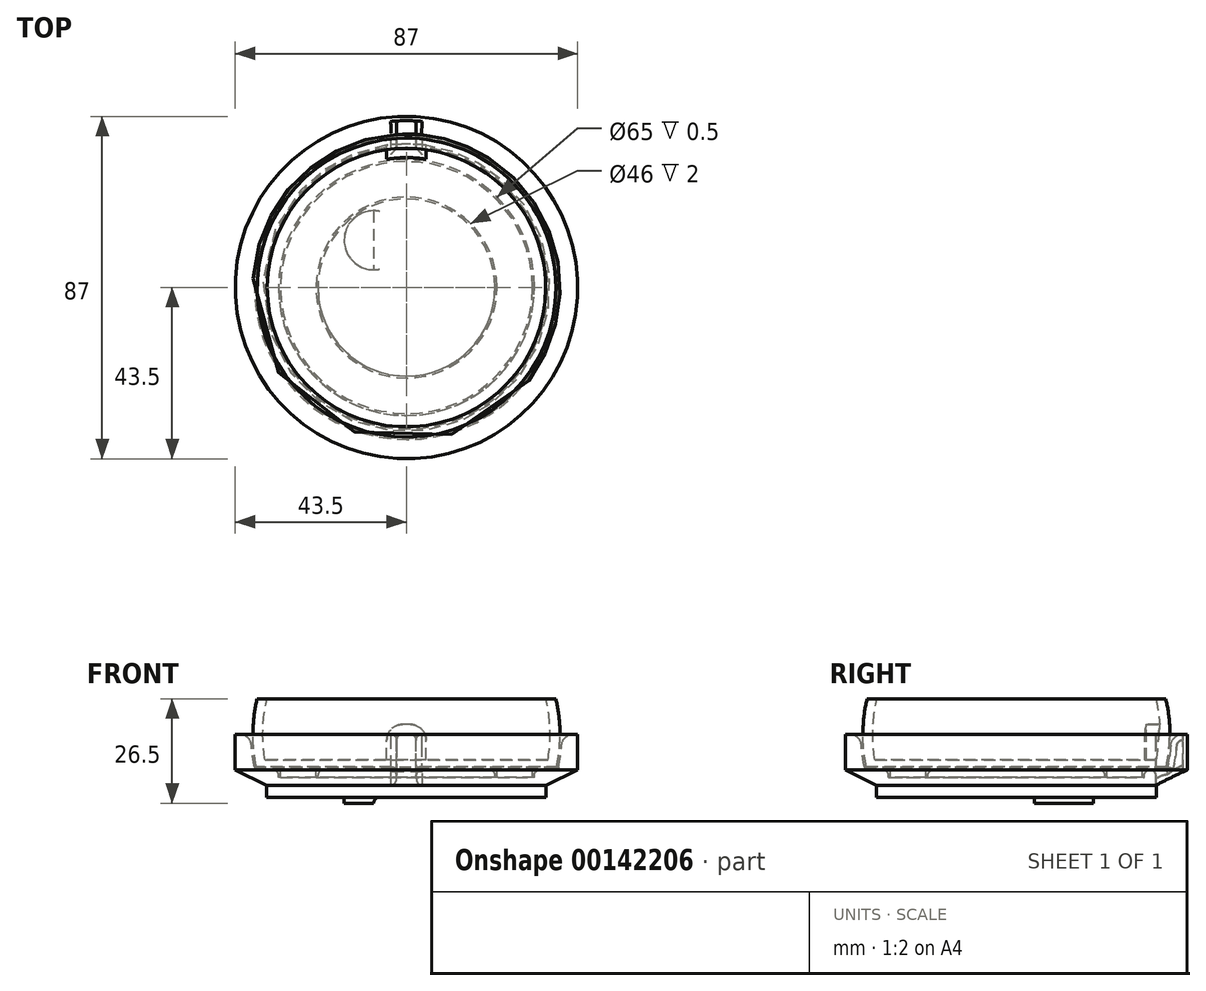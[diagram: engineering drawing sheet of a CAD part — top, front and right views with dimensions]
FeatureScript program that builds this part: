
annotation { "Feature Type Name" : "Feature", "Feature Type Description" : "" }
export const myFeature = defineFeature(function(context is Context, id is Id, definition is map)
    precondition{}
    {
        {
            var Q0;
            Q0=qCreatedBy(makeId("Front.planeOp"),FACE);
            var sketch = newSketch(context, id + "F0", { "sketchPlane" : qUnion([Q0])});
            skArc(sketch, "E0", {"start": v(37.95, -9) * mm, "mid": v(39, 0) * mm, "end": v(37.95, 9) * mm});
            skLineSegment(sketch, "E1", {"start": v(-37.95, 9) * mm, "end": v(37.95, 9) * mm});
            skLineSegment(sketch, "E2.MirrorCS", {"start": v(-37.95, -9) * mm, "end": v(37.95, -9) * mm});
            skArc(sketch, "E3.trimOffspring", {"start": v(-37.95, 9) * mm, "mid": v(-39, 0) * mm, "end": v(-37.95, -9) * mm});
            skLineSegment(sketch, "E4", {"start": v(0, 9) * mm, "end": v(0, -9) * mm});
            skSolve(sketch);
        }
        {
            var Q0;
            {var subQ0=sQuery(id+"F0.wireOp",EDGE,"E0");Q0=makeQuery(id+"F0.imprint","IMPRINT",FACE,{"disambiguationData":[TD([[makeQuery(id+"F0.imprint","IMPRINT",EDGE,{"derivedFrom":subQ0}),1.0]])]});}
            var Q1;
            Q1=sQuery(id+"F0.wireOp",EDGE,"E4");
            revolve(context, id + "F1", {"entities" : qUnion([Q0]), "axis" : qUnion([Q1]), "revolveType" : RevolveType.FULL});
        }
        {
            var Q0;
            Q0=makeQuery(id+"F1.opRevolve","SWEPT_EDGE",EDGE,{"disambiguationData":[OSD([sQuery(id+"F0.wireOp",EDGE,"E0"),sQuery(id+"F0.wireOp",EDGE,"E2.MirrorCS")])]});
            fillet(context, id + "F2", {"entities" : qUnion([Q0]), "radius" : 1 * mm, "tangentPropagation" : true, "allowEdgeOverflow" : false});
        }
        {
            var Q0;
            Q0=makeQuery(id+"F1.opRevolve","SWEPT_FACE",FACE,{"disambiguationData":[OSD([sQuery(id+"F0.wireOp",EDGE,"E2.MirrorCS")])]});
            var sketch = newSketch(context, id + "F3", { "sketchPlane" : qUnion([Q0])});
            skCircle(sketch, "E5.0", {"center": v(0, 0) * mm, "radius": 37.15 * mm});
            skCircle(sketch, "E6", {"center": v(0, 0) * mm, "radius": 23 * mm});
            skCircle(sketch, "E7", {"center": v(0, 0) * mm, "radius": 32 * mm});
            skSolve(sketch);
        }
        {
            var Q0;
            Q0=makeQuery(id+"F3.imprint","IMPRINT",FACE,{"disambiguationData":[TD([[makeQuery(id+"F3.imprint","IMPRINT",EDGE,{"derivedFrom":sQuery(id+"F3.wireOp",EDGE,"E6")}),-1.0]])]});
            extrude(context, id + "F4", {"entities" : qUnion([Q0]), "depth" : 2 * mm});
        }
        {
            var Q0;
            Q0=qCreatedBy(makeId("Front.planeOp"),FACE);
            var sketch = newSketch(context, id + "F5", { "sketchPlane" : qUnion([Q0])});
            skLineSegment(sketch, "E8.0", {"start": v(38.27, -9) * mm, "end": v(0, -9) * mm});
            skLineSegment(sketch, "E9", {"start": v(32.5, -9) * mm, "end": v(32.5, -11) * mm});
            skLineSegment(sketch, "E10.0", {"start": v(32.5, -11) * mm, "end": v(22.5, -11) * mm});
            skLineSegment(sketch, "E11", {"start": v(0, 0) * mm, "end": v(39.5, 0) * mm});
            skLineSegment(sketch, "E12", {"start": v(39.5, 0) * mm, "end": v(43.5, 0) * mm});
            skLineSegment(sketch, "E13", {"start": v(43.5, 0) * mm, "end": v(43.5, -9) * mm});
            skLineSegment(sketch, "E14", {"start": v(0, 0) * mm, "end": v(0, -23) * mm});
            skLineSegment(sketch, "E15", {"start": v(22.5, -9) * mm, "end": v(22.5, -11) * mm});
            skArc(sketch, "E16.0", {"start": v(38.61, -8.32) * mm, "mid": v(39.28, -4.18) * mm, "end": v(39.5, 0) * mm});
            skArc(sketch, "E16.1", {"start": v(38.27, -9) * mm, "mid": v(38.49, -8.68) * mm, "end": v(38.61, -8.32) * mm});
            skPoint(sketch, "E17.orphan", {"position": v(37.15, -9) * mm});
            skLineSegment(sketch, "E18", {"start": v(35.5, -21) * mm, "end": v(35.5, -13) * mm});
            skLineSegment(sketch, "E19", {"start": v(35.5, -21) * mm, "end": v(43.5, -21) * mm});
            skLineSegment(sketch, "E20", {"start": v(43.5, -21) * mm, "end": v(43.5, -23) * mm});
            skLineSegment(sketch, "E21", {"start": v(43.5, -23) * mm, "end": v(0, -23) * mm});
            skPoint(sketch, "E22.visualSharp", {"position": v(35.5, -21) * mm});
            skLineSegment(sketch, "E23", {"start": v(43.5, -9) * mm, "end": v(35.5, -13) * mm});
            skSolve(sketch);
        }
        {
            var Q0;
            {var subQ1=sQuery(id+"F5.wireOp",EDGE,"E9");Q0=makeQuery(id+"F5.imprint","IMPRINT",FACE,{"disambiguationData":[TD([[makeQuery(id+"F5.imprint","IMPRINT",EDGE,{"derivedFrom":subQ1}),1.0]])]});}
            var Q1;
            Q1=sQuery(id+"F5.wireOp",EDGE,"E14");
            revolve(context, id + "F6", {"entities" : qUnion([Q0]), "axis" : qUnion([Q1]), "revolveType" : RevolveType.FULL});
        }
        {
            var Q0;
            Q0=makeQuery(id+"F6.opRevolve","SWEPT_EDGE",EDGE,{"disambiguationData":[OSD([sQuery(id+"F5.wireOp",EDGE,"E12"),sQuery(id+"F5.wireOp",EDGE,"E16.0")])]});
            fillet(context, id + "F7", {"entities" : qUnion([Q0]), "radius" : 3 * mm, "tangentPropagation" : true, "allowEdgeOverflow" : false});
        }
        {
            var Q0;
            Q0=makeQuery(id+"F6.opRevolve","SWEPT_EDGE",EDGE,{"disambiguationData":[OSD([sQuery(id+"F5.wireOp",EDGE,"E8.0"),sQuery(id+"F5.wireOp",EDGE,"E9")])]});
            var Q1;
            Q1=makeQuery(id+"F6.opRevolve","SWEPT_EDGE",EDGE,{"disambiguationData":[OSD([sQuery(id+"F5.wireOp",EDGE,"E8.0"),sQuery(id+"F5.wireOp",EDGE,"E15")])]});
            fillet(context, id + "F8", {"entities" : qUnion([Q0, Q1]), "radius" : 1.5 * mm, "tangentPropagation" : true, "allowEdgeOverflow" : false});
        }
        {
            var Q0;
            Q0=makeQuery(id+"F6.opRevolve","SWEPT_FACE",FACE,{"disambiguationData":[OSD([sQuery(id+"F5.wireOp",EDGE,"E12")])]});
            var sketch = newSketch(context, id + "F9", { "sketchPlane" : qUnion([Q0])});
            skArc(sketch, "E24.0", {"start": v(2.47, 43.43) * mm, "mid": v(-0.02, 43.5) * mm, "end": v(-2.52, 43.43) * mm});
            skLineSegment(sketch, "E25.trimOffspring", {"start": v(-7.5, 31.62) * mm, "end": v(-7.5, -31.62) * mm});
            skLineSegment(sketch, "E26.trimOffspring", {"start": v(7.5, 31.62) * mm, "end": v(7.5, -31.62) * mm});
            skLineSegment(sketch, "E27.left", {"start": v(2.5, 32.4) * mm, "end": v(2.47, 43.43) * mm});
            skLineSegment(sketch, "E27.right", {"start": v(-2.5, 32.4) * mm, "end": v(-2.52, 43.43) * mm});
            skPoint(sketch, "E28.orphan", {"position": v(7.5, 36.76) * mm});
            skArc(sketch, "E29.0", {"start": v(-2.5, 32.4) * mm, "mid": v(-5.01, 32.11) * mm, "end": v(-7.5, 31.62) * mm});
            skArc(sketch, "E30.trimOffspring", {"start": v(7.5, 31.62) * mm, "mid": v(5.01, 32.11) * mm, "end": v(2.5, 32.4) * mm});
            skArc(sketch, "E31.trimOffspring", {"start": v(-7.5, -31.62) * mm, "mid": v(0, -32.5) * mm, "end": v(7.5, -31.62) * mm});
            skCircle(sketch, "E32.0", {"center": v(0, 0) * mm, "radius": 35.5 * mm});
            skSolve(sketch);
        }
        {
            var Q0;
            {var subQ0=sQuery(id+"F9.wireOp",EDGE,"E32.0");var subQ1=sQuery(id+"F9.wireOp",EDGE,"E27.left");var subQ2=makeQuery(id+"F9.imprint","INTERSECT",VERTEX,{"derivedFrom":[subQ1,subQ0]});Q0=makeQuery(id+"F9.imprint","IMPRINT",FACE,{"disambiguationData":[TD([[makeQuery(id+"F9.imprint","IMPRINT",EDGE,{"disambiguationData":[TD([[subQ2,-1.0]])],"derivedFrom":subQ0}),-1.0]])]});}
            var Q1;
            {var subQ0=sQuery(id+"F9.wireOp",EDGE,"E24.0");Q1=makeQuery(id+"F9.imprint","IMPRINT",FACE,{"disambiguationData":[TD([[makeQuery(id+"F9.imprint","IMPRINT",EDGE,{"derivedFrom":subQ0}),1.0]])]});}
            extrude(context, id + "F10", {"entities" : qUnion([Q0, Q1]), "operationType" : NewBodyOperationType.REMOVE, "oppositeDirection" : true, "depth" : 14 * mm});
        }
        {
            var Q0;
            {var subQ0=sQuery(id+"F5.wireOp",EDGE,"E8.0");Q0=makeQuery(id+"F10.boolean.opBoolean","INTERSECT",EDGE,{"derivedFrom":[makeQuery(id+"F6.opRevolve","SWEPT_FACE",FACE,{"disambiguationData":[OSD([subQ0]),TDD([makeQuery(id+"F5.imprint","IMPRINT",EDGE,{"disambiguationData":[TD([[makeQuery(id+"F5.imprint","INTERSECT",VERTEX,{"derivedFrom":[subQ0,sQuery(id+"F5.wireOp",EDGE,"E16.1")]}),-1.0]])],"derivedFrom":subQ0})])]}),makeQuery(id+"F10.opExtrude","SWEPT_FACE",FACE,{"disambiguationData":[OSD([sQuery(id+"F9.wireOp",EDGE,"E32.0")])]})]});}
            var Q1;
            {var subQ0=sQuery(id+"F5.wireOp",EDGE,"E8.0");Q1=makeQuery(id+"F10.boolean.opBoolean","INTERSECT",EDGE,{"derivedFrom":[makeQuery(id+"F6.opRevolve","SWEPT_FACE",FACE,{"disambiguationData":[OSD([subQ0]),TDD([makeQuery(id+"F5.imprint","IMPRINT",EDGE,{"disambiguationData":[TD([[makeQuery(id+"F5.imprint","INTERSECT",VERTEX,{"derivedFrom":[subQ0,sQuery(id+"F5.wireOp",EDGE,"E16.1")]}),-1.0]])],"derivedFrom":subQ0})])]}),makeQuery(id+"F10.opExtrude","SWEPT_FACE",FACE,{"disambiguationData":[OSD([sQuery(id+"F9.wireOp",EDGE,"E27.right")])]})]});}
            var Q2;
            Q2=makeQuery(id+"F10.boolean.opBoolean","INTERSECT",EDGE,{"derivedFrom":[makeQuery(id+"F6.opRevolve","SWEPT_FACE",FACE,{"disambiguationData":[OSD([sQuery(id+"F5.wireOp",EDGE,"E16.1")])]}),makeQuery(id+"F10.opExtrude","SWEPT_FACE",FACE,{"disambiguationData":[OSD([sQuery(id+"F9.wireOp",EDGE,"E27.right")])]})]});
            var Q3;
            Q3=makeQuery(id+"F10.boolean.opBoolean","INTERSECT",EDGE,{"derivedFrom":[makeQuery(id+"F6.opRevolve","SWEPT_FACE",FACE,{"disambiguationData":[OSD([sQuery(id+"F5.wireOp",EDGE,"E16.0")])]}),makeQuery(id+"F10.opExtrude","SWEPT_FACE",FACE,{"disambiguationData":[OSD([sQuery(id+"F9.wireOp",EDGE,"E27.right")])]})]});
            var Q4;
            {var subQ0=sQuery(id+"F5.wireOp",EDGE,"E8.0");Q4=makeQuery(id+"F10.boolean.opBoolean","INTERSECT",EDGE,{"derivedFrom":[makeQuery(id+"F6.opRevolve","SWEPT_FACE",FACE,{"disambiguationData":[OSD([subQ0]),TDD([makeQuery(id+"F5.imprint","IMPRINT",EDGE,{"disambiguationData":[TD([[makeQuery(id+"F5.imprint","INTERSECT",VERTEX,{"derivedFrom":[subQ0,sQuery(id+"F5.wireOp",EDGE,"E16.1")]}),-1.0]])],"derivedFrom":subQ0})])]}),makeQuery(id+"F10.opExtrude","SWEPT_FACE",FACE,{"disambiguationData":[OSD([sQuery(id+"F9.wireOp",EDGE,"E27.left")])]})]});}
            var Q5;
            Q5=makeQuery(id+"F10.boolean.opBoolean","INTERSECT",EDGE,{"derivedFrom":[makeQuery(id+"F6.opRevolve","SWEPT_FACE",FACE,{"disambiguationData":[OSD([sQuery(id+"F5.wireOp",EDGE,"E16.1")])]}),makeQuery(id+"F10.opExtrude","SWEPT_FACE",FACE,{"disambiguationData":[OSD([sQuery(id+"F9.wireOp",EDGE,"E27.left")])]})]});
            var Q6;
            Q6=makeQuery(id+"F10.boolean.opBoolean","INTERSECT",EDGE,{"derivedFrom":[makeQuery(id+"F6.opRevolve","SWEPT_FACE",FACE,{"disambiguationData":[OSD([sQuery(id+"F5.wireOp",EDGE,"E16.0")])]}),makeQuery(id+"F10.opExtrude","SWEPT_FACE",FACE,{"disambiguationData":[OSD([sQuery(id+"F9.wireOp",EDGE,"E27.left")])]})]});
            var Q7;
            Q7=makeQuery(id+"F10.boolean.opBoolean","INTERSECT",EDGE,{"derivedFrom":[makeQuery(id+"F7.opFillet","BLEND_FACE",FACE,{"disambiguationData":[OSD([sQuery(id+"F5.wireOp",EDGE,"E11"),sQuery(id+"F5.wireOp",EDGE,"E12"),sQuery(id+"F5.wireOp",EDGE,"E16.0")])]}),makeQuery(id+"F10.opExtrude","SWEPT_FACE",FACE,{"disambiguationData":[OSD([sQuery(id+"F9.wireOp",EDGE,"E27.left")])]})]});
            var Q8;
            Q8=makeQuery(id+"F10.boolean.opBoolean","COPY",EDGE,{"derivedFrom":makeQuery(id+"F10.opExtrude","CAP_EDGE",EDGE,{"disambiguationData":[OSD([sQuery(id+"F9.wireOp",EDGE,"E27.left")])],"isStart":true})});
            var Q9;
            Q9=makeQuery(id+"F10.boolean.opBoolean","INTERSECT",EDGE,{"derivedFrom":[makeQuery(id+"F6.opRevolve","SWEPT_FACE",FACE,{"disambiguationData":[OSD([sQuery(id+"F5.wireOp",EDGE,"E23")])]}),makeQuery(id+"F10.opExtrude","SWEPT_FACE",FACE,{"disambiguationData":[OSD([sQuery(id+"F9.wireOp",EDGE,"E27.right")])]})]});
            var Q10;
            Q10=makeQuery(id+"F10.boolean.opBoolean","INTERSECT",EDGE,{"derivedFrom":[makeQuery(id+"F6.opRevolve","SWEPT_FACE",FACE,{"disambiguationData":[OSD([sQuery(id+"F5.wireOp",EDGE,"E23")])]}),makeQuery(id+"F10.opExtrude","SWEPT_FACE",FACE,{"disambiguationData":[OSD([sQuery(id+"F9.wireOp",EDGE,"E27.left")])]})]});
            var Q11;
            Q11=makeQuery(id+"F10.boolean.opBoolean","INTERSECT",EDGE,{"derivedFrom":[makeQuery(id+"F7.opFillet","BLEND_FACE",FACE,{"disambiguationData":[OSD([sQuery(id+"F5.wireOp",EDGE,"E11"),sQuery(id+"F5.wireOp",EDGE,"E12"),sQuery(id+"F5.wireOp",EDGE,"E16.0")])]}),makeQuery(id+"F10.opExtrude","SWEPT_FACE",FACE,{"disambiguationData":[OSD([sQuery(id+"F9.wireOp",EDGE,"E27.right")])]})]});
            var Q12;
            Q12=makeQuery(id+"F10.boolean.opBoolean","COPY",EDGE,{"derivedFrom":makeQuery(id+"F10.opExtrude","CAP_EDGE",EDGE,{"disambiguationData":[OSD([sQuery(id+"F9.wireOp",EDGE,"E27.right")])],"isStart":true})});
            fillet(context, id + "F11", {"entities" : qUnion([Q0, Q1, Q2, Q3, Q4, Q5, Q6, Q7, Q8, Q9, Q10, Q11, Q12]), "radius" : 1.5 * mm, "tangentPropagation" : true, "allowEdgeOverflow" : false});
        }
        {
            var Q0;
            Q0=makeQuery(id+"F6.opRevolve","SWEPT_FACE",FACE,{"disambiguationData":[OSD([sQuery(id+"F5.wireOp",EDGE,"E19")])]});
            var sketch = newSketch(context, id + "F12", { "sketchPlane" : qUnion([Q0])});
            skCircle(sketch, "E33.0", {"center": v(0, 0) * mm, "radius": 43.5 * mm});
            skCircle(sketch, "E34.0", {"center": v(0, 0) * mm, "radius": 35.5 * mm});
            skLineSegment(sketch, "E35", {"start": v(2.5, 35.41) * mm, "end": v(2.5, 43.43) * mm});
            skLineSegment(sketch, "E36", {"start": v(-2.5, 35.41) * mm, "end": v(-2.5, 43.43) * mm});
            skSolve(sketch);
        }
        {
            var Q0;
            {var subQ0=sQuery(id+"F12.wireOp",EDGE,"E35");Q0=makeQuery(id+"F12.imprint","IMPRINT",FACE,{"disambiguationData":[TD([[makeQuery(id+"F12.imprint","IMPRINT",EDGE,{"derivedFrom":subQ0}),1.0]])]});}
            extrude(context, id + "F13", {"entities" : qUnion([Q0]), "operationType" : NewBodyOperationType.REMOVE, "oppositeDirection" : true, "depth" : 25 * mm});
        }
        {
            var Q0;
            Q0=makeQuery(id+"F6.opRevolve","SWEPT_FACE",FACE,{"disambiguationData":[OSD([sQuery(id+"F5.wireOp",EDGE,"E21")])]});
            var sketch = newSketch(context, id + "F14", { "sketchPlane" : qUnion([Q0])});
            skLineSegment(sketch, "E37", {"start": v(-2.5, -43.43) * mm, "end": v(-2.5, -28.43) * mm});
            skLineSegment(sketch, "E38", {"start": v(2.5, -43.43) * mm, "end": v(2.5, -28.43) * mm});
            skLineSegment(sketch, "E39", {"start": v(-2.5, -43.43) * mm, "end": v(2.5, -43.43) * mm});
            skPoint(sketch, "E40", {"position": v(0, -35.5) * mm});
            skLineSegment(sketch, "E41", {"start": v(0, -43.43) * mm, "end": v(0, 10.29) * mm, "construction": true});
            skArc(sketch, "E42", {"start": v(-8.32, -20.49) * mm, "mid": v(-4.92, -27.2) * mm, "end": v(2.5, -28.43) * mm});
            skLineSegment(sketch, "E43", {"start": v(-8.33, -20.49) * mm, "end": v(-8.33, -3.56) * mm});
            skLineSegment(sketch, "E44", {"start": v(8.32, -20.49) * mm, "end": v(8.32, -3.56) * mm});
            skLineSegment(sketch, "E45", {"start": v(-8.32, -3.56) * mm, "end": v(-6.25, -3.56) * mm});
            skLineSegment(sketch, "E46", {"start": v(-6.25, -3.56) * mm, "end": v(-6.25, 8.94) * mm});
            skLineSegment(sketch, "E47", {"start": v(-6.25, 8.94) * mm, "end": v(6.25, 8.94) * mm});
            skLineSegment(sketch, "E48", {"start": v(6.25, 8.94) * mm, "end": v(6.25, -3.56) * mm});
            skLineSegment(sketch, "E49.trimOffspring", {"start": v(6.25, -3.56) * mm, "end": v(8.32, -3.56) * mm});
            skArc(sketch, "E50.trimOffspring", {"start": v(2.5, -28.43) * mm, "mid": v(6.71, -25.41) * mm, "end": v(8.32, -20.49) * mm});
            skArc(sketch, "E51", {"start": v(-8.33, -4.52) * mm, "mid": v(-15.82, -12.02) * mm, "end": v(-8.32, -19.52) * mm});
            skSolve(sketch);
        }
        {
            var Q0;
            {var subQ0=sQuery(id+"F14.wireOp",EDGE,"E43");Q0=makeQuery(id+"F14.imprint","IMPRINT",FACE,{"disambiguationData":[TD([[makeQuery(id+"F14.imprint","IMPRINT",EDGE,{"derivedFrom":subQ0}),-1.0]])]});}
            extrude(context, id + "F15", {"entities" : qUnion([Q0]), "operationType" : NewBodyOperationType.REMOVE, "oppositeDirection" : true, "depth" : 7 * mm});
        }
        {
            var Q0;
            {var subQ1=makeQuery(id+"F13.boolean.opBoolean","INTERSECT",EDGE,{"derivedFrom":[makeQuery(id+"F6.opRevolve","SWEPT_FACE",FACE,{"disambiguationData":[OSD([sQuery(id+"F5.wireOp",EDGE,"E21")])]}),makeQuery(id+"F13.opExtrude","SWEPT_FACE",FACE,{"disambiguationData":[OSD([sQuery(id+"F12.wireOp",EDGE,"E34.0")])]})]});Q0=makeQuery(id+"F14.imprint","IMPRINT",FACE,{"disambiguationData":[TD([[makeQuery(id+"F14.imprint","IMPRINT",EDGE,{"derivedFrom":subQ1}),1.0]])]});}
            extrude(context, id + "F16", {"entities" : qUnion([Q0]), "operationType" : NewBodyOperationType.REMOVE, "oppositeDirection" : true, "depth" : 6 * mm});
        }
        {
            var Q0;
            {var subQ0=sQuery(id+"F14.wireOp",EDGE,"E51");Q0=makeQuery(id+"F14.imprint","IMPRINT",FACE,{"disambiguationData":[TD([[makeQuery(id+"F14.imprint","IMPRINT",EDGE,{"derivedFrom":subQ0}),1.0]])]});}
            extrude(context, id + "F17", {"entities" : qUnion([Q0]), "oppositeDirection" : true, "depth" : 5.5 * mm});
        }
        {
            var Q0;
            Q0=qCreatedBy(makeId("Front.planeOp"),FACE);
            var sketch = newSketch(context, id + "F18", { "sketchPlane" : qUnion([Q0])});
            skLineSegment(sketch, "E52.0", {"start": v(-8.32, -17.5) * mm, "end": v(-15.82, -17.5) * mm});
            skLineSegment(sketch, "E53.0", {"start": v(-8.32, -17.5) * mm, "end": v(-8.32, -23) * mm});
            skLineSegment(sketch, "E54.0", {"start": v(-8.32, -23) * mm, "end": v(-15.82, -23) * mm});
            skLineSegment(sketch, "E55", {"start": v(-15.82, -23) * mm, "end": v(-15.82, -17.5) * mm});
            skLineSegment(sketch, "E56", {"start": v(-8.32, -17.5) * mm, "end": v(-15.82, -22) * mm});
            skSolve(sketch);
        }
        {
            var Q0;
            {var subQ0=sQuery(id+"F18.wireOp",EDGE,"E52.0");Q0=makeQuery(id+"F18.imprint","IMPRINT",FACE,{"disambiguationData":[TD([[makeQuery(id+"F18.imprint","IMPRINT",EDGE,{"derivedFrom":subQ0}),1.0]])]});}
            var Q1;
            Q1=makeQuery(id+"F17.opExtrude","SWEPT_FACE",FACE,{"disambiguationData":[OSD([sQuery(id+"F14.wireOp",EDGE,"E51")])]});
            extrude(context, id + "F19", {"entities" : qUnion([Q0]), "operationType" : NewBodyOperationType.REMOVE, "endBound" : BoundingType.THROUGH_ALL, "oppositeDirection" : true, "endBoundEntityFace" : qUnion([Q1]), "depth" : 25 * mm});
        }
        {
            var Q0;
            Q0=makeQuery(id+"F17.opExtrude","SWEPT_BODY",BODY,{"disambiguationData":[OSD([sQuery(id+"F14.wireOp",EDGE,"E43"),sQuery(id+"F14.wireOp",EDGE,"E51")])]});
            var Q1;
            Q1=makeQuery(id+"F6.opRevolve","SWEPT_BODY",BODY,{"disambiguationData":[OSD([sQuery(id+"F5.wireOp",EDGE,"E8.0"),sQuery(id+"F5.wireOp",EDGE,"E9"),sQuery(id+"F5.wireOp",EDGE,"E10.0"),sQuery(id+"F5.wireOp",EDGE,"E12"),sQuery(id+"F5.wireOp",EDGE,"E13"),sQuery(id+"F5.wireOp",EDGE,"E14"),sQuery(id+"F5.wireOp",EDGE,"E15"),sQuery(id+"F5.wireOp",EDGE,"E16.0"),sQuery(id+"F5.wireOp",EDGE,"E16.1"),sQuery(id+"F5.wireOp",EDGE,"E18"),sQuery(id+"F5.wireOp",EDGE,"E19"),sQuery(id+"F5.wireOp",EDGE,"E20"),sQuery(id+"F5.wireOp",EDGE,"E21"),sQuery(id+"F5.wireOp",EDGE,"E23")])]});
            booleanBodies(context, id + "F20", {"operationType" : BooleanOperationType.SUBTRACTION, "tools" : qUnion([Q0]), "targets" : qUnion([Q1])});
        }
        {
            var Q0;
            Q0=makeQuery(id+"F16.boolean.opBoolean","MERGE",EDGE,{"derivedFrom":[makeQuery(id+"F13.boolean.opBoolean","INTERSECT",EDGE,{"derivedFrom":[makeQuery(id+"F6.opRevolve","SWEPT_FACE",FACE,{"disambiguationData":[OSD([sQuery(id+"F5.wireOp",EDGE,"E21")])]}),makeQuery(id+"F13.opExtrude","SWEPT_FACE",FACE,{"disambiguationData":[OSD([sQuery(id+"F12.wireOp",EDGE,"E36")])]})]}),makeQuery(id+"F16.opExtrude","CAP_EDGE",EDGE,{"disambiguationData":[OSD([sQuery(id+"F14.wireOp",EDGE,"E37")])],"isStart":true})]});
            var Q1;
            {var subQ0=sQuery(id+"F14.wireOp",EDGE,"E50.trimOffspring");var subQ1=sQuery(id+"F14.wireOp",EDGE,"E42");Q1=makeQuery(id+"F16.boolean.opBoolean","SPLIT",EDGE,{"disambiguationData":[TD([makeQuery(id+"F13.boolean.opBoolean","COPY",FACE,{"derivedFrom":makeQuery(id+"F13.opExtrude","SWEPT_FACE",FACE,{"disambiguationData":[OSD([sQuery(id+"F12.wireOp",EDGE,"E36")])]})})])],"derivedFrom":makeQuery(id+"F15.boolean.opBoolean","COPY",EDGE,{"derivedFrom":makeQuery(id+"F15.opExtrude","CAP_EDGE",EDGE,{"disambiguationData":[OSD([subQ1,subQ0])],"isStart":true})})});}
            var Q2;
            Q2=makeQuery(id+"F15.boolean.opBoolean","COPY",EDGE,{"derivedFrom":makeQuery(id+"F15.opExtrude","CAP_EDGE",EDGE,{"disambiguationData":[OSD([sQuery(id+"F14.wireOp",EDGE,"E43")])],"isStart":true})});
            var Q3;
            Q3=makeQuery(id+"F15.boolean.opBoolean","COPY",EDGE,{"derivedFrom":makeQuery(id+"F15.opExtrude","CAP_EDGE",EDGE,{"disambiguationData":[OSD([sQuery(id+"F14.wireOp",EDGE,"E45")])],"isStart":true})});
            var Q4;
            Q4=makeQuery(id+"F15.boolean.opBoolean","COPY",EDGE,{"derivedFrom":makeQuery(id+"F15.opExtrude","CAP_EDGE",EDGE,{"disambiguationData":[OSD([sQuery(id+"F14.wireOp",EDGE,"E46")])],"isStart":true})});
            var Q5;
            Q5=makeQuery(id+"F15.boolean.opBoolean","COPY",EDGE,{"derivedFrom":makeQuery(id+"F15.opExtrude","CAP_EDGE",EDGE,{"disambiguationData":[OSD([sQuery(id+"F14.wireOp",EDGE,"E47")])],"isStart":true})});
            var Q6;
            Q6=makeQuery(id+"F15.boolean.opBoolean","COPY",EDGE,{"derivedFrom":makeQuery(id+"F15.opExtrude","CAP_EDGE",EDGE,{"disambiguationData":[OSD([sQuery(id+"F14.wireOp",EDGE,"E48")])],"isStart":true})});
            var Q7;
            Q7=makeQuery(id+"F15.boolean.opBoolean","COPY",EDGE,{"derivedFrom":makeQuery(id+"F15.opExtrude","CAP_EDGE",EDGE,{"disambiguationData":[OSD([sQuery(id+"F14.wireOp",EDGE,"E49.trimOffspring")])],"isStart":true})});
            var Q8;
            Q8=makeQuery(id+"F15.boolean.opBoolean","COPY",EDGE,{"derivedFrom":makeQuery(id+"F15.opExtrude","CAP_EDGE",EDGE,{"disambiguationData":[OSD([sQuery(id+"F14.wireOp",EDGE,"E44")])],"isStart":true})});
            var Q9;
            {var subQ0=sQuery(id+"F14.wireOp",EDGE,"E50.trimOffspring");var subQ1=sQuery(id+"F14.wireOp",EDGE,"E42");Q9=makeQuery(id+"F16.boolean.opBoolean","SPLIT",EDGE,{"disambiguationData":[TD([makeQuery(id+"F13.boolean.opBoolean","COPY",FACE,{"derivedFrom":makeQuery(id+"F13.opExtrude","SWEPT_FACE",FACE,{"disambiguationData":[OSD([sQuery(id+"F12.wireOp",EDGE,"E35")])]})})])],"derivedFrom":makeQuery(id+"F15.boolean.opBoolean","COPY",EDGE,{"derivedFrom":makeQuery(id+"F15.opExtrude","CAP_EDGE",EDGE,{"disambiguationData":[OSD([subQ1,subQ0])],"isStart":true})})});}
            var Q10;
            Q10=makeQuery(id+"F16.boolean.opBoolean","MERGE",EDGE,{"derivedFrom":[makeQuery(id+"F13.boolean.opBoolean","INTERSECT",EDGE,{"derivedFrom":[makeQuery(id+"F6.opRevolve","SWEPT_FACE",FACE,{"disambiguationData":[OSD([sQuery(id+"F5.wireOp",EDGE,"E21")])]}),makeQuery(id+"F13.opExtrude","SWEPT_FACE",FACE,{"disambiguationData":[OSD([sQuery(id+"F12.wireOp",EDGE,"E35")])]})]}),makeQuery(id+"F16.opExtrude","CAP_EDGE",EDGE,{"disambiguationData":[OSD([sQuery(id+"F14.wireOp",EDGE,"E38")])],"isStart":true})]});
            var Q11;
            Q11=makeQuery(id+"F15.boolean.opBoolean","COPY",EDGE,{"derivedFrom":makeQuery(id+"F15.opExtrude","CAP_EDGE",EDGE,{"disambiguationData":[OSD([sQuery(id+"F14.wireOp",EDGE,"E46")])],"isStart":false})});
            var Q12;
            Q12=makeQuery(id+"F15.boolean.opBoolean","COPY",EDGE,{"derivedFrom":makeQuery(id+"F15.opExtrude","CAP_EDGE",EDGE,{"disambiguationData":[OSD([sQuery(id+"F14.wireOp",EDGE,"E43")])],"isStart":false})});
            var Q13;
            Q13=makeQuery(id+"F15.boolean.opBoolean","COPY",EDGE,{"derivedFrom":makeQuery(id+"F15.opExtrude","CAP_EDGE",EDGE,{"disambiguationData":[OSD([sQuery(id+"F14.wireOp",EDGE,"E45")])],"isStart":false})});
            var Q14;
            Q14=makeQuery(id+"F15.boolean.opBoolean","COPY",EDGE,{"derivedFrom":makeQuery(id+"F15.opExtrude","CAP_EDGE",EDGE,{"disambiguationData":[OSD([sQuery(id+"F14.wireOp",EDGE,"E42"),sQuery(id+"F14.wireOp",EDGE,"E50.trimOffspring")])],"isStart":false})});
            var Q15;
            Q15=makeQuery(id+"F15.boolean.opBoolean","COPY",EDGE,{"derivedFrom":makeQuery(id+"F15.opExtrude","CAP_EDGE",EDGE,{"disambiguationData":[OSD([sQuery(id+"F14.wireOp",EDGE,"E44")])],"isStart":false})});
            var Q16;
            Q16=makeQuery(id+"F15.boolean.opBoolean","COPY",EDGE,{"derivedFrom":makeQuery(id+"F15.opExtrude","CAP_EDGE",EDGE,{"disambiguationData":[OSD([sQuery(id+"F14.wireOp",EDGE,"E48")])],"isStart":false})});
            var Q17;
            Q17=makeQuery(id+"F15.boolean.opBoolean","COPY",EDGE,{"derivedFrom":makeQuery(id+"F15.opExtrude","CAP_EDGE",EDGE,{"disambiguationData":[OSD([sQuery(id+"F14.wireOp",EDGE,"E49.trimOffspring")])],"isStart":false})});
            var Q18;
            Q18=makeQuery(id+"F15.boolean.opBoolean","COPY",EDGE,{"derivedFrom":makeQuery(id+"F15.opExtrude","CAP_EDGE",EDGE,{"disambiguationData":[OSD([sQuery(id+"F14.wireOp",EDGE,"E47")])],"isStart":false})});
            var Q19;
            Q19=makeQuery(id+"F16.boolean.opBoolean","COPY",EDGE,{"derivedFrom":makeQuery(id+"F16.opExtrude","CAP_EDGE",EDGE,{"disambiguationData":[OSD([sQuery(id+"F5.wireOp",EDGE,"E21"),sQuery(id+"F12.wireOp",EDGE,"E34.0")])],"isStart":false})});
            var Q20;
            Q20=makeQuery(id+"F16.boolean.opBoolean","COPY",EDGE,{"derivedFrom":makeQuery(id+"F16.opExtrude","SWEPT_EDGE",EDGE,{"disambiguationData":[OSD([sQuery(id+"F5.wireOp",EDGE,"E21"),sQuery(id+"F12.wireOp",EDGE,"E34.0"),sQuery(id+"F14.wireOp",EDGE,"E38")])]})});
            var Q21;
            Q21=makeQuery(id+"F16.boolean.opBoolean","COPY",EDGE,{"derivedFrom":makeQuery(id+"F16.opExtrude","SWEPT_EDGE",EDGE,{"disambiguationData":[OSD([sQuery(id+"F5.wireOp",EDGE,"E21"),sQuery(id+"F12.wireOp",EDGE,"E34.0"),sQuery(id+"F14.wireOp",EDGE,"E37")])]})});
            var Q22;
            Q22=makeQuery(id+"F10.boolean.opBoolean","INTERSECT",EDGE,{"derivedFrom":[makeQuery(id+"F6.opRevolve","SWEPT_FACE",FACE,{"disambiguationData":[OSD([sQuery(id+"F5.wireOp",EDGE,"E18")])]}),makeQuery(id+"F10.opExtrude","CAP_FACE",FACE,{"disambiguationData":[OSD([sQuery(id+"F9.wireOp",EDGE,"E24.0"),sQuery(id+"F9.wireOp",EDGE,"E25.trimOffspring"),sQuery(id+"F9.wireOp",EDGE,"E26.trimOffspring"),sQuery(id+"F9.wireOp",EDGE,"E27.left"),sQuery(id+"F9.wireOp",EDGE,"E27.right"),sQuery(id+"F9.wireOp",EDGE,"E29.0"),sQuery(id+"F9.wireOp",EDGE,"E30.trimOffspring"),sQuery(id+"F9.wireOp",EDGE,"E31.trimOffspring")])],"isStart":false})]});
            var Q23;
            Q23=makeQuery(id+"F11.opFillet","BLEND_EDGE",EDGE,{"blendedFrom":[makeQuery(id+"F10.boolean.opBoolean","COPY",EDGE,{"derivedFrom":makeQuery(id+"F10.opExtrude","CAP_EDGE",EDGE,{"disambiguationData":[OSD([sQuery(id+"F9.wireOp",EDGE,"E27.right")])],"isStart":false})}),makeQuery(id+"F6.opRevolve","SWEPT_FACE",FACE,{"disambiguationData":[OSD([sQuery(id+"F5.wireOp",EDGE,"E18")])]})],"blendedInto":[makeQuery(id+"F6.opRevolve","SWEPT_FACE",FACE,{"disambiguationData":[OSD([sQuery(id+"F5.wireOp",EDGE,"E18")])]})]});
            var Q24;
            Q24=makeQuery(id+"F11.opFillet","BLEND_EDGE",EDGE,{"blendedFrom":[makeQuery(id+"F10.boolean.opBoolean","COPY",EDGE,{"derivedFrom":makeQuery(id+"F10.opExtrude","CAP_EDGE",EDGE,{"disambiguationData":[OSD([sQuery(id+"F9.wireOp",EDGE,"E27.left")])],"isStart":false})}),makeQuery(id+"F6.opRevolve","SWEPT_FACE",FACE,{"disambiguationData":[OSD([sQuery(id+"F5.wireOp",EDGE,"E18")])]})],"blendedInto":[makeQuery(id+"F6.opRevolve","SWEPT_FACE",FACE,{"disambiguationData":[OSD([sQuery(id+"F5.wireOp",EDGE,"E18")])]})]});
            var Q25;
            Q25=makeQuery(id+"F13.boolean.opBoolean","COPY",EDGE,{"derivedFrom":makeQuery(id+"F13.opExtrude","CAP_EDGE",EDGE,{"disambiguationData":[OSD([sQuery(id+"F12.wireOp",EDGE,"E35")])],"isStart":true})});
            var Q26;
            Q26=makeQuery(id+"F13.boolean.opBoolean","COPY",EDGE,{"derivedFrom":makeQuery(id+"F13.opExtrude","CAP_EDGE",EDGE,{"disambiguationData":[OSD([sQuery(id+"F12.wireOp",EDGE,"E36")])],"isStart":true})});
            var Q27;
            Q27=makeQuery(id+"F20.opBoolean","COPY",EDGE,{"derivedFrom":makeQuery(id+"F17.opExtrude","CAP_EDGE",EDGE,{"disambiguationData":[OSD([sQuery(id+"F14.wireOp",EDGE,"E51")])],"isStart":true})});
            fillet(context, id + "F21", {"entities" : qUnion([Q0, Q1, Q2, Q3, Q4, Q5, Q6, Q7, Q8, Q9, Q10, Q11, Q12, Q13, Q14, Q15, Q16, Q17, Q18, Q19, Q20, Q21, Q22, Q23, Q24, Q25, Q26, Q27]), "radius" : 1.5 * mm, "tangentPropagation" : true, "allowEdgeOverflow" : false});
        }
        {
            var Q0;
            Q0=makeQuery(id+"F1.opRevolve","SWEPT_FACE",FACE,{"disambiguationData":[OSD([sQuery(id+"F0.wireOp",EDGE,"E1")])]});
            shell(context, id + "F22", {"entities" : qUnion([Q0]), "thickness" : 2.5 * mm});
        }
    });
